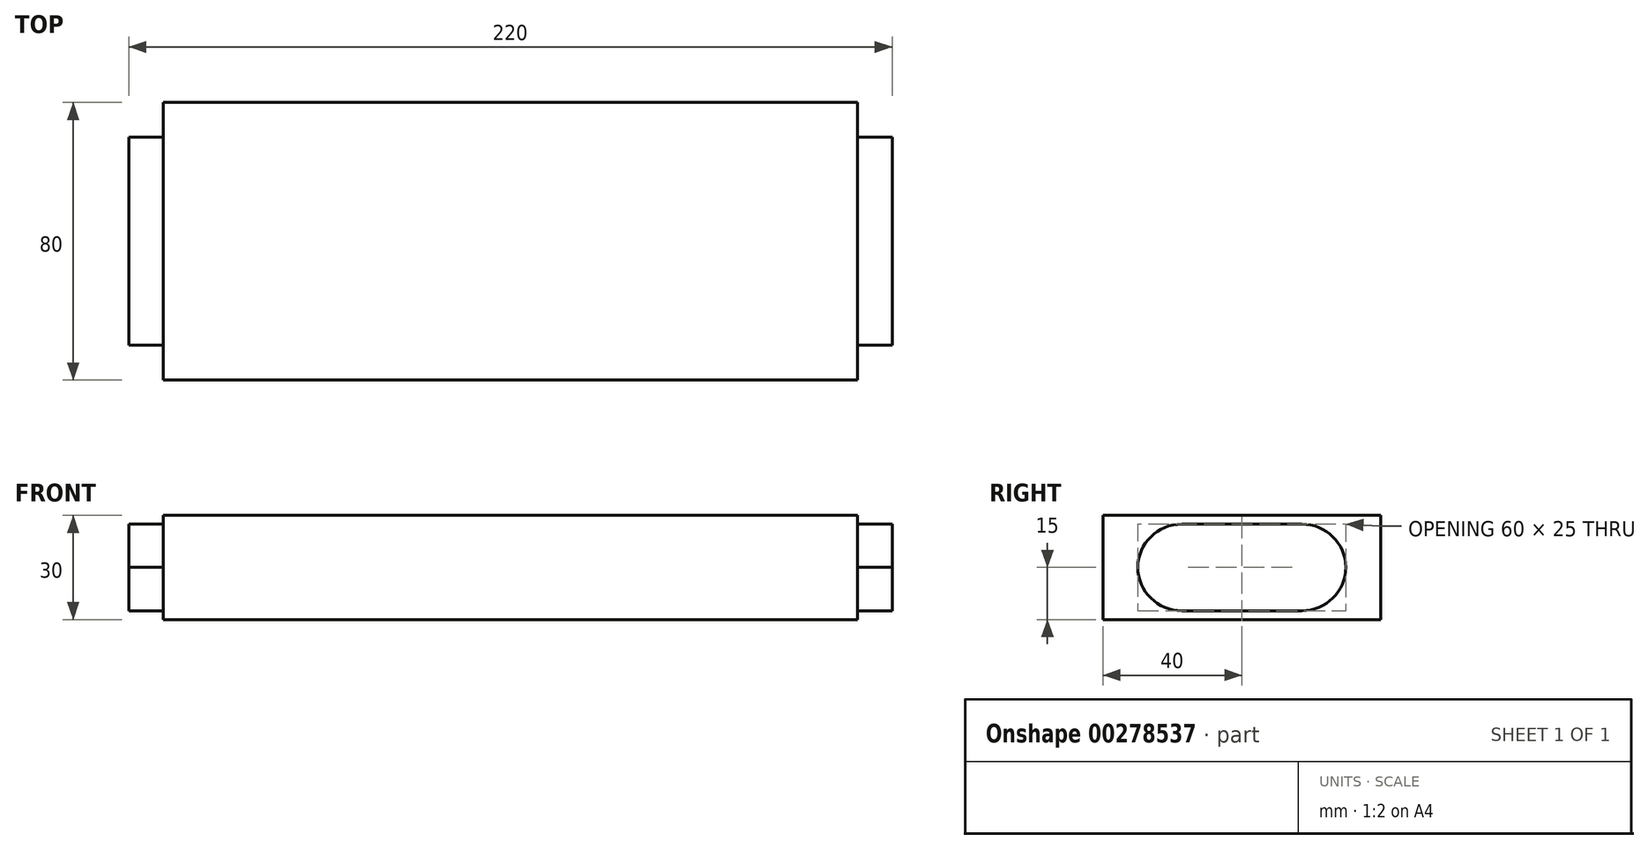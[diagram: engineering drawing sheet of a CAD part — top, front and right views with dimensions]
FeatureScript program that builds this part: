
annotation { "Feature Type Name" : "Feature", "Feature Type Description" : "" }
export const myFeature = defineFeature(function(context is Context, id is Id, definition is map)
    precondition{}
    {
        {
            var Q0;
            Q0=qCreatedBy(makeId("Top.planeOp"),FACE);
            var sketch = newSketch(context, id + "F0", { "sketchPlane" : qUnion([Q0])});
            skLineSegment(sketch, "E0.bottom", {"start": v(100, -40) * mm, "end": v(-100, -40) * mm});
            skLineSegment(sketch, "E0.top", {"start": v(100, 40) * mm, "end": v(-100, 40) * mm});
            skLineSegment(sketch, "E0.left", {"start": v(100, -40) * mm, "end": v(100, 40) * mm});
            skLineSegment(sketch, "E0.right", {"start": v(-100, -40) * mm, "end": v(-100, 40) * mm});
            skPoint(sketch, "E0.middle", {"position": v(0, 0) * mm});
            skSolve(sketch);
        }
        {
            var Q0;
            Q0=makeQuery(id+"F0.imprint","IMPRINT",FACE,{"disambiguationData":[TD([[makeQuery(id+"F0.imprint","IMPRINT",EDGE,{"derivedFrom":sQuery(id+"F0.wireOp",EDGE,"E0.bottom")}),-1.0]])]});
            extrude(context, id + "F1", {"entities" : qUnion([Q0]), "depth" : 30 * mm});
        }
        {
            var Q0;
            Q0=makeQuery(id+"F1.opExtrude","SWEPT_FACE",FACE,{"disambiguationData":[OSD([sQuery(id+"F0.wireOp",EDGE,"E0.right")])]});
            var sketch = newSketch(context, id + "F2", { "sketchPlane" : qUnion([Q0])});
            skLineSegment(sketch, "E1.bottom", {"start": v(30, 27.5) * mm, "end": v(-30, 27.5) * mm});
            skLineSegment(sketch, "E1.top", {"start": v(30, 2.5) * mm, "end": v(-30, 2.5) * mm});
            skLineSegment(sketch, "E1.left", {"start": v(30, 27.5) * mm, "end": v(30, 2.5) * mm});
            skLineSegment(sketch, "E1.right", {"start": v(-30, 27.5) * mm, "end": v(-30, 2.5) * mm});
            skPoint(sketch, "E1.middle", {"position": v(0, 15) * mm});
            skLineSegment(sketch, "E2", {"start": v(-40, 15) * mm, "end": v(40, 15) * mm, "construction": true});
            skSolve(sketch);
        }
        {
            var Q0;
            Q0=makeQuery(id+"F2.imprint","IMPRINT",FACE,{"disambiguationData":[TD([[makeQuery(id+"F2.imprint","IMPRINT",EDGE,{"derivedFrom":sQuery(id+"F2.wireOp",EDGE,"E1.bottom")}),1.0]])]});
            extrude(context, id + "F3", {"entities" : qUnion([Q0]), "operationType" : NewBodyOperationType.ADD, "depth" : 10 * mm});
        }
        {
            var Q0;
            Q0=makeQuery(id+"F1.opExtrude","SWEPT_FACE",FACE,{"disambiguationData":[OSD([sQuery(id+"F0.wireOp",EDGE,"E0.left")])]});
            var sketch = newSketch(context, id + "F4", { "sketchPlane" : qUnion([Q0])});
            skLineSegment(sketch, "E3.bottom", {"start": v(30, 2.5) * mm, "end": v(-30, 2.5) * mm});
            skLineSegment(sketch, "E3.top", {"start": v(30, 27.5) * mm, "end": v(-30, 27.5) * mm});
            skLineSegment(sketch, "E3.left", {"start": v(30, 2.5) * mm, "end": v(30, 27.5) * mm});
            skLineSegment(sketch, "E3.right", {"start": v(-30, 2.5) * mm, "end": v(-30, 27.5) * mm});
            skPoint(sketch, "E3.middle", {"position": v(0, 15) * mm});
            skLineSegment(sketch, "E4", {"start": v(-40, 15) * mm, "end": v(40, 15) * mm, "construction": true});
            skSolve(sketch);
        }
        {
            var Q0;
            Q0=makeQuery(id+"F4.imprint","IMPRINT",FACE,{"disambiguationData":[TD([[makeQuery(id+"F4.imprint","IMPRINT",EDGE,{"derivedFrom":sQuery(id+"F4.wireOp",EDGE,"E3.bottom")}),-1.0]])]});
            extrude(context, id + "F5", {"entities" : qUnion([Q0]), "operationType" : NewBodyOperationType.ADD, "depth" : 10 * mm});
        }
        {
            var Q0;
            Q0=makeQuery(id+"F5.opExtrude","SWEPT_EDGE",EDGE,{"disambiguationData":[OSD([sQuery(id+"F4.wireOp",EDGE,"E3.top"),sQuery(id+"F4.wireOp",EDGE,"E3.right")])]});
            var Q1;
            Q1=makeQuery(id+"F5.opExtrude","SWEPT_EDGE",EDGE,{"disambiguationData":[OSD([sQuery(id+"F4.wireOp",EDGE,"E3.bottom"),sQuery(id+"F4.wireOp",EDGE,"E3.right")])]});
            var Q2;
            Q2=makeQuery(id+"F5.opExtrude","SWEPT_EDGE",EDGE,{"disambiguationData":[OSD([sQuery(id+"F4.wireOp",EDGE,"E3.top"),sQuery(id+"F4.wireOp",EDGE,"E3.left")])]});
            var Q3;
            Q3=makeQuery(id+"F5.opExtrude","SWEPT_EDGE",EDGE,{"disambiguationData":[OSD([sQuery(id+"F4.wireOp",EDGE,"E3.bottom"),sQuery(id+"F4.wireOp",EDGE,"E3.left")])]});
            var Q4;
            Q4=makeQuery(id+"F3.opExtrude","SWEPT_EDGE",EDGE,{"disambiguationData":[OSD([sQuery(id+"F2.wireOp",EDGE,"E1.bottom"),sQuery(id+"F2.wireOp",EDGE,"E1.right")])]});
            var Q5;
            Q5=makeQuery(id+"F3.opExtrude","SWEPT_EDGE",EDGE,{"disambiguationData":[OSD([sQuery(id+"F2.wireOp",EDGE,"E1.bottom"),sQuery(id+"F2.wireOp",EDGE,"E1.left")])]});
            var Q6;
            Q6=makeQuery(id+"F3.opExtrude","SWEPT_EDGE",EDGE,{"disambiguationData":[OSD([sQuery(id+"F2.wireOp",EDGE,"E1.top"),sQuery(id+"F2.wireOp",EDGE,"E1.left")])]});
            var Q7;
            Q7=makeQuery(id+"F3.opExtrude","SWEPT_EDGE",EDGE,{"disambiguationData":[OSD([sQuery(id+"F2.wireOp",EDGE,"E1.top"),sQuery(id+"F2.wireOp",EDGE,"E1.right")])]});
            fillet(context, id + "F6", {"entities" : qUnion([Q0, Q1, Q2, Q3, Q4, Q5, Q6, Q7]), "radius" : 12.7 * mm, "tangentPropagation" : true, "allowEdgeOverflow" : false});
        }
    });
